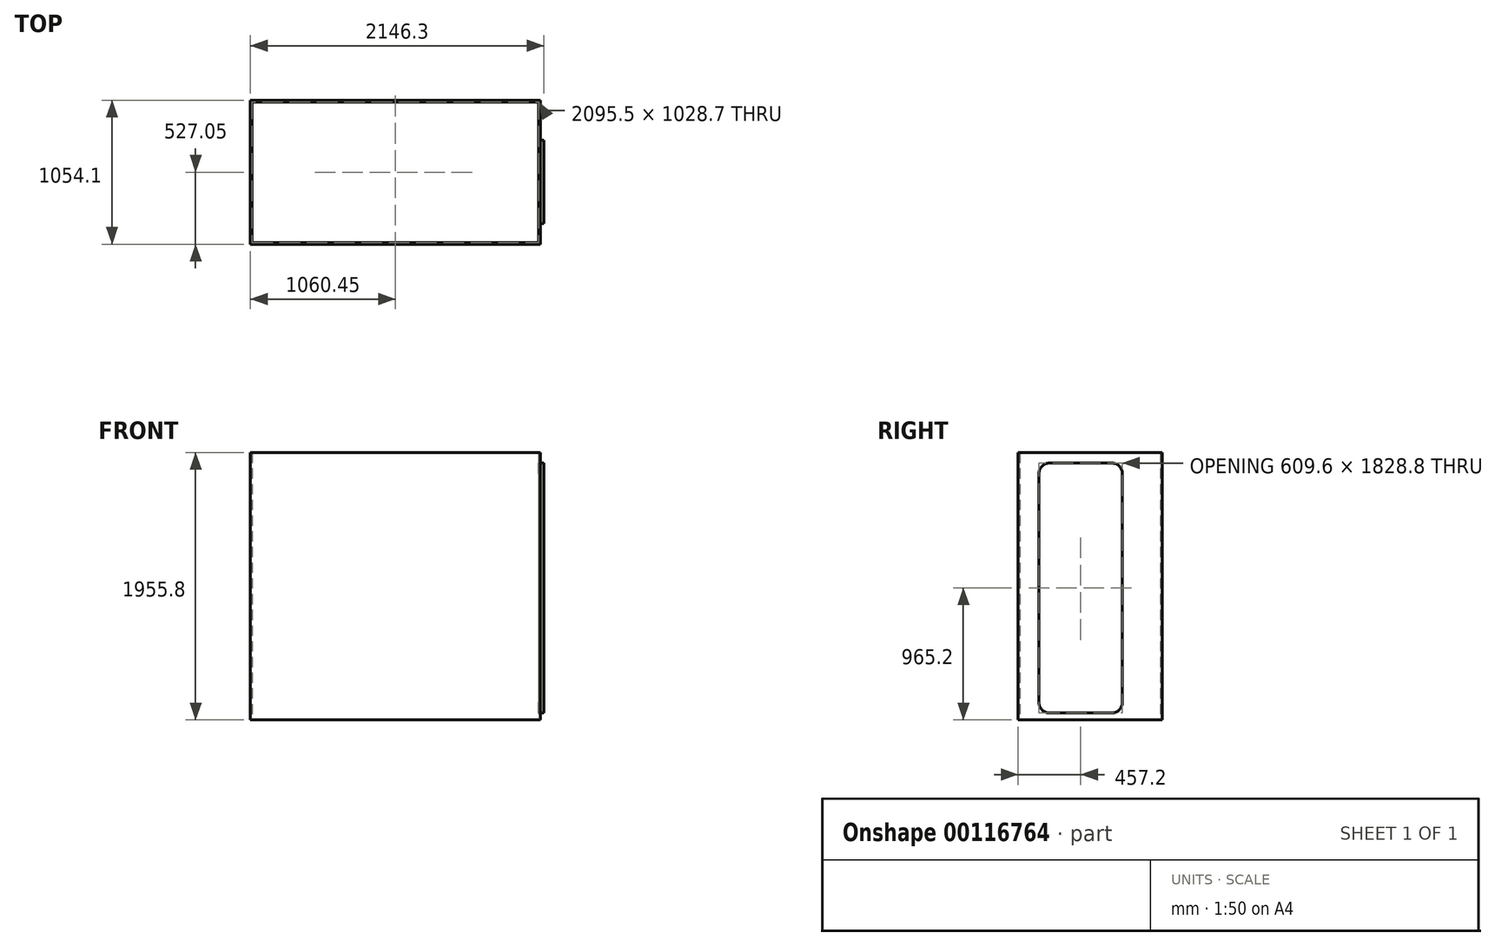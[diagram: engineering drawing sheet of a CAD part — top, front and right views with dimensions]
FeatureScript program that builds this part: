
annotation { "Feature Type Name" : "Feature", "Feature Type Description" : "" }
export const myFeature = defineFeature(function(context is Context, id is Id, definition is map)
    precondition{}
    {
        {
            var Q0;
            Q0=qCreatedBy(makeId("Top.planeOp"),FACE);
            var sketch = newSketch(context, id + "F0", { "sketchPlane" : qUnion([Q0])});
            skLineSegment(sketch, "E0.bottom", {"start": v(0, 0) * mm, "end": v(2120.9, 0) * mm});
            skLineSegment(sketch, "E0.top", {"start": v(0, 1054.1) * mm, "end": v(2120.9, 1054.1) * mm});
            skLineSegment(sketch, "E0.left", {"start": v(0, 0) * mm, "end": v(0, 1054.1) * mm});
            skLineSegment(sketch, "E0.right", {"start": v(2120.9, 0) * mm, "end": v(2120.9, 1054.1) * mm});
            skLineSegment(sketch, "E1.bottom", {"start": v(2108.2, 12.7) * mm, "end": v(12.7, 12.7) * mm});
            skLineSegment(sketch, "E1.top", {"start": v(2108.2, 1041.4) * mm, "end": v(12.7, 1041.4) * mm});
            skLineSegment(sketch, "E1.left", {"start": v(2108.2, 12.7) * mm, "end": v(2108.2, 1041.4) * mm});
            skLineSegment(sketch, "E1.right", {"start": v(12.7, 12.7) * mm, "end": v(12.7, 1041.4) * mm});
            skPoint(sketch, "E1.middle", {"position": v(1060.45, 527.05) * mm});
            skPoint(sketch, "E1.middle.positionSnap0", {"position": v(1060.45, 1054.1) * mm});
            skPoint(sketch, "E1.centerSnap0", {"position": v(1060.45, 1054.1) * mm});
            skSolve(sketch);
        }
        {
            var Q0;
            Q0=qSketchRegion(id+"F0",true);
            extrude(context, id + "F1", {"entities" : qUnion([Q0]), "depth" : 1955.8 * mm});
        }
        {
            var Q0;
            Q0=makeQuery(id+"F1.opExtrude","SWEPT_FACE",FACE,{"disambiguationData":[OSD([sQuery(id+"F0.wireOp",EDGE,"E0.right")])]});
            var sketch = newSketch(context, id + "F2", { "sketchPlane" : qUnion([Q0])});
            skLineSegment(sketch, "E2", {"start": v(0, 0) * mm, "end": v(1054.1, 0) * mm});
            skLineSegment(sketch, "E3", {"start": v(0, 0) * mm, "end": v(152.4, 0) * mm});
            skLineSegment(sketch, "E4", {"start": v(152.4, 0) * mm, "end": v(152.4, 50.8) * mm});
            skLineSegment(sketch, "E5", {"start": v(228.6, 50.8) * mm, "end": v(685.8, 50.8) * mm});
            skLineSegment(sketch, "E6", {"start": v(762, 127) * mm, "end": v(762, 1803.4) * mm});
            skLineSegment(sketch, "E7", {"start": v(685.8, 1879.6) * mm, "end": v(228.6, 1879.6) * mm});
            skLineSegment(sketch, "E8", {"start": v(152.4, 1803.4) * mm, "end": v(152.4, 127) * mm});
            skPoint(sketch, "E9.visualSharp", {"position": v(152.4, 1879.6) * mm});
            skArc(sketch, "E9.filletArc", {"start": v(228.6, 1879.6) * mm, "mid": v(174.72, 1857.28) * mm, "end": v(152.4, 1803.4) * mm});
            skPoint(sketch, "E10.visualSharp", {"position": v(762, 1879.6) * mm});
            skArc(sketch, "E10.filletArc", {"start": v(762, 1803.4) * mm, "mid": v(739.68, 1857.28) * mm, "end": v(685.8, 1879.6) * mm});
            skPoint(sketch, "E11.visualSharp", {"position": v(152.4, 50.8) * mm});
            skArc(sketch, "E11.filletArc", {"start": v(152.4, 127) * mm, "mid": v(174.72, 73.12) * mm, "end": v(228.6, 50.8) * mm});
            skPoint(sketch, "E12.visualSharp", {"position": v(762, 50.8) * mm});
            skArc(sketch, "E12.filletArc", {"start": v(685.8, 50.8) * mm, "mid": v(739.68, 73.12) * mm, "end": v(762, 127) * mm});
            skSolve(sketch);
        }
        {
            var Q0;
            Q0=qSketchRegion(id+"F2",true);
            extrude(context, id + "F3", {"entities" : qUnion([Q0]), "operationType" : NewBodyOperationType.REMOVE, "endBound" : BoundingType.UP_TO_NEXT, "oppositeDirection" : true, "depth" : 25.4 * mm});
        }
        {
            var Q0;
            Q0=makeQuery(id+"F1.opExtrude","SWEPT_FACE",FACE,{"disambiguationData":[OSD([sQuery(id+"F0.wireOp",EDGE,"E0.right")])]});
            var sketch = newSketch(context, id + "F4", { "sketchPlane" : qUnion([Q0])});
            skLineSegment(sketch, "E13", {"start": v(152.4, 1803.4) * mm, "end": v(152.4, 127) * mm});
            skLineSegment(sketch, "E14", {"start": v(228.6, 50.8) * mm, "end": v(685.8, 50.8) * mm});
            skLineSegment(sketch, "E15", {"start": v(762, 1803.4) * mm, "end": v(762, 127) * mm});
            skLineSegment(sketch, "E16", {"start": v(228.6, 1879.6) * mm, "end": v(685.8, 1879.6) * mm});
            skArc(sketch, "E17", {"start": v(228.6, 1879.6) * mm, "mid": v(174.72, 1857.28) * mm, "end": v(152.4, 1803.4) * mm});
            skArc(sketch, "E18", {"start": v(762, 1803.4) * mm, "mid": v(739.68, 1857.28) * mm, "end": v(685.8, 1879.6) * mm});
            skArc(sketch, "E19", {"start": v(685.8, 50.8) * mm, "mid": v(739.68, 73.12) * mm, "end": v(762, 127) * mm});
            skArc(sketch, "E20", {"start": v(152.4, 127) * mm, "mid": v(174.72, 73.12) * mm, "end": v(228.6, 50.8) * mm});
            skSolve(sketch);
        }
        {
            var Q0;
            Q0=makeQuery(id+"F4.imprint","IMPRINT",FACE,{"disambiguationData":[TD([[makeQuery(id+"F4.imprint","IMPRINT",EDGE,{"derivedFrom":sQuery(id+"F4.wireOp",EDGE,"E13")}),1.0]])]});
            extrude(context, id + "F5", {"entities" : qUnion([Q0]), "depth" : 25.4 * mm});
        }
    });
